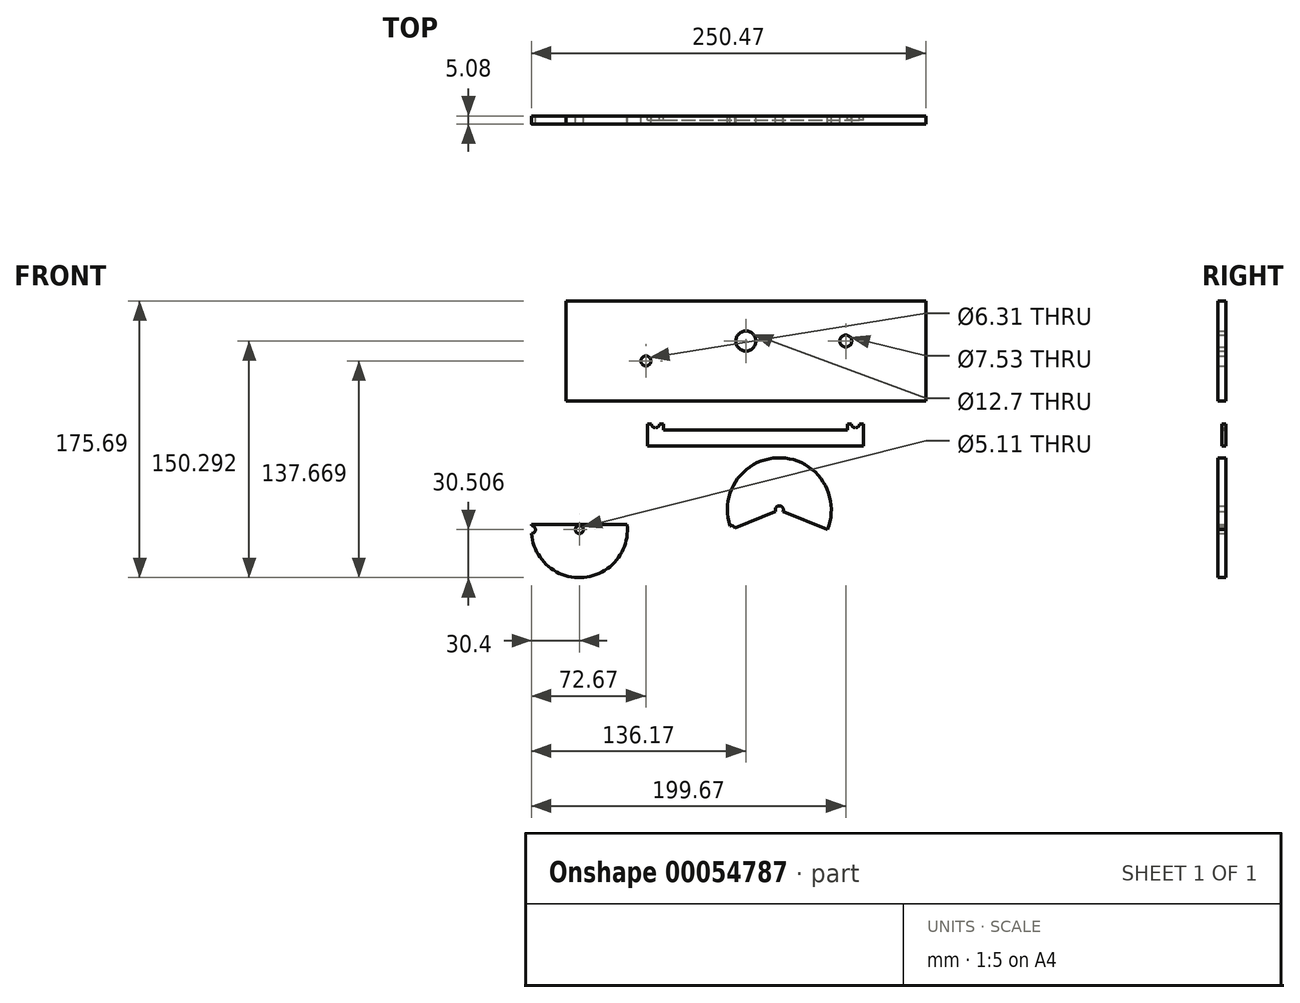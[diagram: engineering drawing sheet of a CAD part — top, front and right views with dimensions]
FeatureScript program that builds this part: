
annotation { "Feature Type Name" : "Feature", "Feature Type Description" : "" }
export const myFeature = defineFeature(function(context is Context, id is Id, definition is map)
    precondition{}
    {
        {
            var Q0;
            Q0=qCreatedBy(makeId("Front.planeOp"),FACE);
            var sketch = newSketch(context, id + "F0", { "sketchPlane" : qUnion([Q0])});
            skCircle(sketch, "E0", {"center": v(0, 0) * mm, "radius": 33.02 * mm});
            skLineSegment(sketch, "E1", {"start": v(0, 0) * mm, "end": v(-45.52, -18.85) * mm});
            skLineSegment(sketch, "E2", {"start": v(47.99, -19.88) * mm, "end": v(0, 0) * mm});
            skPoint(sketch, "E3", {"position": v(-30.5, -12.64) * mm});
            skPoint(sketch, "E4", {"position": v(30.5, -12.64) * mm});
            skPoint(sketch, "E5", {"position": v(-127, -12.62) * mm});
            skCircle(sketch, "E6", {"center": v(-127, -12.62) * mm, "radius": 30.5 * mm});
            skLineSegment(sketch, "E7", {"start": v(-127, -12.62) * mm, "end": v(30.5, -12.64) * mm, "construction": true});
            skPoint(sketch, "E8", {"position": v(-96.5, -12.63) * mm});
            skLineSegment(sketch, "E9", {"start": v(-30.5, -12.64) * mm, "end": v(-127, -12.62) * mm, "construction": true});
            skLineSegment(sketch, "E10", {"start": v(-127, -12.62) * mm, "end": v(-157.5, -12.62) * mm, "construction": true});
            skPoint(sketch, "E11", {"position": v(-157.5, -12.62) * mm});
            skPoint(sketch, "E12", {"position": v(-60.96, 0) * mm});
            skPoint(sketch, "E13", {"position": v(60.96, 0) * mm});
            skCircle(sketch, "E14", {"center": v(-60.96, 0) * mm, "radius": 7.62 * mm});
            skCircle(sketch, "E15", {"center": v(60.96, 0) * mm, "radius": 7.62 * mm});
            skPoint(sketch, "E16", {"position": v(12.7, -30.48) * mm});
            skPoint(sketch, "E17", {"position": v(-107.42, 10.77) * mm});
            skLineSegment(sketch, "E18", {"start": v(-107.42, 10.77) * mm, "end": v(12.7, -30.48) * mm, "construction": true});
            skPoint(sketch, "E19", {"position": v(-113.93, -40.19) * mm});
            skLineSegment(sketch, "E20", {"start": v(-113.93, -40.19) * mm, "end": v(12.7, -30.48) * mm, "construction": true});
            skCircle(sketch, "E21", {"center": v(-30.5, -12.64) * mm, "radius": 2.56 * mm});
            skCircle(sketch, "E22", {"center": v(-157.5, -12.62) * mm, "radius": 2.56 * mm});
            skCircle(sketch, "E23", {"center": v(0, 0) * mm, "radius": 2.56 * mm});
            skCircle(sketch, "E24", {"center": v(-127, -12.62) * mm, "radius": 2.56 * mm});
            skLineSegment(sketch, "E25.bottom", {"start": v(-160.68, -9.44) * mm, "end": v(-27.33, -9.44) * mm});
            skLineSegment(sketch, "E25.top", {"start": v(-160.68, -15.8) * mm, "end": v(-27.33, -15.8) * mm});
            skLineSegment(sketch, "E25.left", {"start": v(-160.68, -9.44) * mm, "end": v(-160.68, -15.8) * mm});
            skLineSegment(sketch, "E25.right", {"start": v(-27.33, -9.44) * mm, "end": v(-27.33, -15.8) * mm});
            skSolve(sketch);
        }
        {
            var Q0;
            {var subQ5=sQuery(id+"F0.wireOp",EDGE,"E6");var subQ7=makeQuery(id+"F0.imprint","INTERSECT",VERTEX,{"derivedFrom":[subQ5,sQuery(id+"F0.wireOp",EDGE,"E18")]});Q0=makeQuery(id+"F0.imprint","IMPRINT",FACE,{"disambiguationData":[TD([[makeQuery(id+"F0.imprint","IMPRINT",EDGE,{"disambiguationData":[TD([[subQ7,-1.0]])],"derivedFrom":subQ5}),1.0]])]});}
            var Q1;
            {var subQ3=sQuery(id+"F0.wireOp",EDGE,"E6");var subQ5=makeQuery(id+"F0.imprint","INTERSECT",VERTEX,{"derivedFrom":[subQ3,sQuery(id+"F0.wireOp",EDGE,"E20")]});Q1=makeQuery(id+"F0.imprint","IMPRINT",FACE,{"disambiguationData":[TD([[makeQuery(id+"F0.imprint","IMPRINT",EDGE,{"disambiguationData":[TD([[subQ5,1.0]])],"derivedFrom":subQ3}),1.0]])]});}
            var Q2;
            {var subQ5=sQuery(id+"F0.wireOp",EDGE,"E9");var subQ6=sQuery(id+"F0.wireOp",EDGE,"E6");var subQ7=makeQuery(id+"F0.imprint","INTERSECT",VERTEX,{"derivedFrom":[subQ6,subQ5]});Q2=makeQuery(id+"F0.imprint","IMPRINT",FACE,{"disambiguationData":[TD([[makeQuery(id+"F0.imprint","IMPRINT",EDGE,{"disambiguationData":[TD([[subQ7,-1.0]])],"derivedFrom":subQ6}),1.0]])]});}
            var Q3;
            {var subQ6=sQuery(id+"F0.wireOp",EDGE,"E6");var subQ9=sQuery(id+"F0.wireOp",EDGE,"E25.top");var subQ11=makeQuery(id+"F0.imprint","INTERSECT",VERTEX,{"disambiguationData":[OD(0.0)],"derivedFrom":[subQ6,subQ9]});Q3=makeQuery(id+"F0.imprint","IMPRINT",FACE,{"disambiguationData":[TD([[makeQuery(id+"F0.imprint","IMPRINT",EDGE,{"disambiguationData":[TD([[subQ11,1.0]])],"derivedFrom":subQ6}),1.0]])]});}
            var Q4;
            {var subQ0=sQuery(id+"F0.wireOp",EDGE,"E25.bottom");var subQ1=sQuery(id+"F0.wireOp",EDGE,"E6");var subQ2=makeQuery(id+"F0.imprint","INTERSECT",VERTEX,{"disambiguationData":[OD(0.0)],"derivedFrom":[subQ1,subQ0]});Q4=makeQuery(id+"F0.imprint","IMPRINT",FACE,{"disambiguationData":[TD([[makeQuery(id+"F0.imprint","IMPRINT",EDGE,{"disambiguationData":[TD([[subQ2,1.0]])],"derivedFrom":subQ1}),1.0]])]});}
            var Q5;
            {var subQ0=sQuery(id+"F0.wireOp",EDGE,"E25.top");var subQ1=sQuery(id+"F0.wireOp",EDGE,"E6");var subQ2=makeQuery(id+"F0.imprint","INTERSECT",VERTEX,{"disambiguationData":[OD(0.0)],"derivedFrom":[subQ1,subQ0]});Q5=makeQuery(id+"F0.imprint","IMPRINT",FACE,{"disambiguationData":[TD([[makeQuery(id+"F0.imprint","IMPRINT",EDGE,{"disambiguationData":[TD([[subQ2,-1.0]])],"derivedFrom":subQ1}),1.0]])]});}
            extrude(context, id + "F1", {"entities" : qUnion([Q0, Q1, Q2, Q3, Q4, Q5]), "depth" : 5.08 * mm});
        }
        {
            var Q0;
            {var subQ3=sQuery(id+"F0.wireOp",EDGE,"E23");var subQ7=sQuery(id+"F0.wireOp",EDGE,"E1");var subQ8=makeQuery(id+"F0.imprint","INTERSECT",VERTEX,{"derivedFrom":[subQ7,subQ3]});Q0=makeQuery(id+"F0.imprint","IMPRINT",FACE,{"disambiguationData":[TD([[makeQuery(id+"F0.imprint","IMPRINT",EDGE,{"disambiguationData":[TD([[subQ8,-1.0]])],"derivedFrom":subQ7}),-1.0]])]});}
            var Q1;
            {var subQ1=sQuery(id+"F0.wireOp",EDGE,"E0");var subQ7=sQuery(id+"F0.wireOp",EDGE,"E25.bottom");var subQ9=makeQuery(id+"F0.imprint","INTERSECT",VERTEX,{"derivedFrom":[subQ1,subQ7]});Q1=makeQuery(id+"F0.imprint","IMPRINT",FACE,{"disambiguationData":[TD([[makeQuery(id+"F0.imprint","IMPRINT",EDGE,{"disambiguationData":[TD([[subQ9,-1.0]])],"derivedFrom":subQ1}),1.0]])]});}
            extrude(context, id + "F2", {"entities" : qUnion([Q0, Q1]), "depth" : 5.08 * mm});
        }
        {
            var Q0;
            Q0=qCreatedBy(makeId("Front.planeOp"),FACE);
            var sketch = newSketch(context, id + "F3", { "sketchPlane" : qUnion([Q0])});
            skCircle(sketch, "E26", {"center": v(-78.63, 54.63) * mm, "radius": 2.54 * mm});
            skCircle(sketch, "E27", {"center": v(48.37, 54.63) * mm, "radius": 2.54 * mm});
            skLineSegment(sketch, "E28.bottom", {"start": v(-83.71, 59.7) * mm, "end": v(53.45, 59.7) * mm, "construction": true});
            skLineSegment(sketch, "E28.top", {"start": v(-83.71, 49.55) * mm, "end": v(53.45, 49.55) * mm, "construction": true});
            skLineSegment(sketch, "E28.left", {"start": v(-83.71, 59.7) * mm, "end": v(-83.71, 49.55) * mm, "construction": true});
            skLineSegment(sketch, "E28.right", {"start": v(53.45, 59.7) * mm, "end": v(53.45, 49.55) * mm, "construction": true});
            skPoint(sketch, "E29", {"position": v(-78.63, 59.7) * mm});
            skPoint(sketch, "E30", {"position": v(48.37, 59.7) * mm});
            skPoint(sketch, "E31", {"position": v(-15.13, 59.7) * mm});
            skCircle(sketch, "E32", {"center": v(-78.63, 54.63) * mm, "radius": 5.08 * mm});
            skCircle(sketch, "E33", {"center": v(48.37, 54.63) * mm, "radius": 5.08 * mm});
            skArc(sketch, "E34", {"start": v(-78.43, 59.7) * mm, "mid": v(-15.13, 57.17) * mm, "end": v(48.16, 59.7) * mm, "construction": true});
            skArc(sketch, "E35", {"start": v(-79.04, 49.56) * mm, "mid": v(-15.13, 47) * mm, "end": v(48.77, 49.56) * mm, "construction": true});
            skLineSegment(sketch, "E36", {"start": v(-78.63, 54.63) * mm, "end": v(-78.63, 50.82) * mm});
            skLineSegment(sketch, "E37", {"start": v(-73.55, 50.82) * mm, "end": v(43.29, 50.82) * mm});
            skLineSegment(sketch, "E38", {"start": v(48.37, 54.63) * mm, "end": v(48.37, 50.82) * mm});
            skLineSegment(sketch, "E39.bottom", {"start": v(-83.71, 54.63) * mm, "end": v(-73.55, 54.63) * mm});
            skLineSegment(sketch, "E39.left", {"start": v(-83.71, 54.63) * mm, "end": v(-83.71, 40.66) * mm});
            skLineSegment(sketch, "E39.right", {"start": v(-73.55, 54.63) * mm, "end": v(-73.55, 50.82) * mm});
            skLineSegment(sketch, "E40.bottom", {"start": v(53.45, 54.63) * mm, "end": v(43.29, 54.63) * mm});
            skLineSegment(sketch, "E40.left", {"start": v(53.45, 54.63) * mm, "end": v(53.45, 40.66) * mm});
            skLineSegment(sketch, "E40.right", {"start": v(43.29, 54.63) * mm, "end": v(43.29, 50.82) * mm});
            skLineSegment(sketch, "E41", {"start": v(-83.71, 40.66) * mm, "end": v(53.45, 40.66) * mm});
            skPoint(sketch, "E42.orphan", {"position": v(53.45, 33.43) * mm});
            skSolve(sketch);
        }
        {
            var Q0;
            Q0=makeQuery(id+"F3.imprint","IMPRINT",FACE,{"disambiguationData":[TD([[makeQuery(id+"F3.imprint","IMPRINT",EDGE,{"derivedFrom":sQuery(id+"F3.wireOp",EDGE,"E26")}),-1.0]])]});
            var Q1;
            {var subQ0=sQuery(id+"F3.wireOp",EDGE,"E35");Q1=makeQuery(id+"F3.imprint","IMPRINT",FACE,{"disambiguationData":[TD([[makeQuery(id+"F3.imprint","IMPRINT",EDGE,{"derivedFrom":subQ0}),1.0]])]});}
            var Q2;
            Q2=makeQuery(id+"F3.imprint","IMPRINT",FACE,{"disambiguationData":[TD([[makeQuery(id+"F3.imprint","IMPRINT",EDGE,{"derivedFrom":sQuery(id+"F3.wireOp",EDGE,"E27")}),-1.0]])]});
            var Q3;
            Q3=makeQuery(id+"F3.imprint","IMPRINT",FACE,{"disambiguationData":[TD([[makeQuery(id+"F3.imprint","IMPRINT",EDGE,{"derivedFrom":sQuery(id+"F3.wireOp",EDGE,"E37")}),-1.0]])]});
            var Q4;
            {var subQ0=sQuery(id+"F3.wireOp",EDGE,"E39.bottom");var subQ1=sQuery(id+"F3.wireOp",EDGE,"E26");var subQ2=makeQuery(id+"F3.imprint","INTERSECT",VERTEX,{"disambiguationData":[OD(0.0)],"derivedFrom":[subQ1,subQ0]});Q4=makeQuery(id+"F3.imprint","IMPRINT",FACE,{"disambiguationData":[TD([[makeQuery(id+"F3.imprint","IMPRINT",EDGE,{"disambiguationData":[TD([[subQ2,1.0]])],"derivedFrom":subQ1}),-1.0]])]});}
            var Q5;
            {var subQ0=sQuery(id+"F3.wireOp",EDGE,"E40.bottom");var subQ1=sQuery(id+"F3.wireOp",EDGE,"E27");var subQ2=makeQuery(id+"F3.imprint","INTERSECT",VERTEX,{"disambiguationData":[OD(0.0)],"derivedFrom":[subQ1,subQ0]});Q5=makeQuery(id+"F3.imprint","IMPRINT",FACE,{"disambiguationData":[TD([[makeQuery(id+"F3.imprint","IMPRINT",EDGE,{"disambiguationData":[TD([[subQ2,1.0]])],"derivedFrom":subQ1}),-1.0]])]});}
            extrude(context, id + "F4", {"entities" : qUnion([Q0, Q1, Q2, Q3, Q4, Q5]), "depth" : 2.54 * mm});
        }
        {
            var Q0;
            Q0=qCreatedBy(makeId("Front.planeOp"),FACE);
            var sketch = newSketch(context, id + "F5", { "sketchPlane" : qUnion([Q0])});
            skLineSegment(sketch, "E43.bottom", {"start": v(-135.53, 132.56) * mm, "end": v(93.07, 132.56) * mm});
            skLineSegment(sketch, "E43.top", {"start": v(-135.53, 69.14) * mm, "end": v(93.07, 69.14) * mm});
            skLineSegment(sketch, "E43.left", {"start": v(-135.53, 132.56) * mm, "end": v(-135.53, 69.14) * mm});
            skLineSegment(sketch, "E43.right", {"start": v(93.07, 132.56) * mm, "end": v(93.07, 69.14) * mm});
            skCircle(sketch, "E44", {"center": v(-84.73, 94.54) * mm, "radius": 3.16 * mm});
            skCircle(sketch, "E45", {"center": v(42.27, 107.16) * mm, "radius": 3.77 * mm});
            skCircle(sketch, "E46", {"center": v(-21.23, 107.16) * mm, "radius": 6.35 * mm});
            skSolve(sketch);
        }
        {
            var Q0;
            Q0=makeQuery(id+"F5.imprint","IMPRINT",FACE,{"disambiguationData":[TD([[makeQuery(id+"F5.imprint","IMPRINT",EDGE,{"derivedFrom":sQuery(id+"F5.wireOp",EDGE,"E43.bottom")}),-1.0]])]});
            extrude(context, id + "F6", {"entities" : qUnion([Q0]), "depth" : 5.08 * mm});
        }
    });
